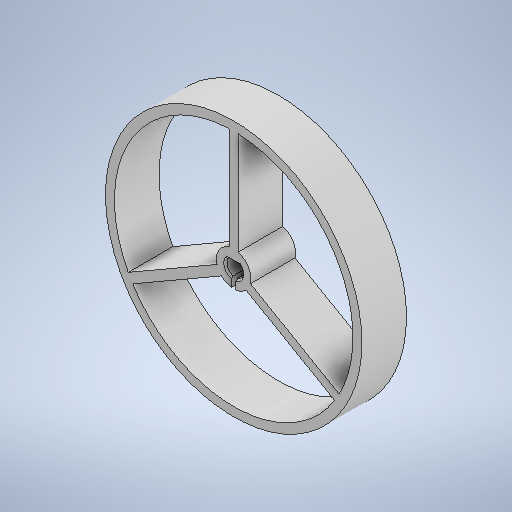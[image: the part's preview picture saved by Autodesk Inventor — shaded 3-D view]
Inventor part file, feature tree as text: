
AUTODESK INVENTOR PART (.ipt)
format: ipt  version: 2025.3 (Build 293356000, 356)  size: 312,320 bytes
history: native  units: mm
features: other x1, extrude x1, pattern_circular x1, chamfer x1
ambient origin geometry x8: Origin, YZ Plane, XZ Plane, XY Plane, X Axis, Y Axis, Z Axis, Center Point
bodies: Body1 (feature_tree)
feature tree (4):
  other  "ソリッド1"
  extrude  "スポーク"  Depth=1.05mm
  pattern_circular  "円形状パターン1"  [2 undecoded]
  chamfer  "面取り1"  Distance=8.0mm
note: 2 required parameter values undecoded (feature->parameter linkage not recoverable at this tier; creation-order binding heuristic only, values carry confidence <= 0.55)
